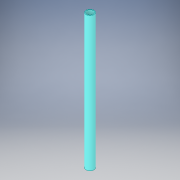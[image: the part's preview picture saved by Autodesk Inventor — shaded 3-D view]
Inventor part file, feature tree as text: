
AUTODESK INVENTOR PART (.ipt)
format: ipt  version: 2018 (Build 220112000, 112)  size: 92,672 bytes
history: native  units: in
note: dims shown in document units (in); Inventor stores cm internally (conversion verified against a paired STEP export)
features: extrude x1, sketch x1
ambient origin geometry x8: Origin, YZ Plane, XZ Plane, XY Plane, X Axis, Y Axis, Z Axis, Center Point
bodies: Solid1 (feature_tree)
feature tree (2):
  extrude  "Extrusion1"  Depth=6.329in
  sketch  "Sketch1"  dims[d0=0.375in d1=0.31in d2=6.329in d3=0.0in]
